# Revit family: Zumtobel PANOS 3 Surface-Mounted R150
name_source: partatom
category: Lighting Fixtures
units: mm (PartAtom-declared; Revit-internal decimal feet)

## family parameters
Cut with Voids When Loaded = Yes
Host = Face
Light Source = Yes
Maintain Annotation Orientation = No
Part Type = Normal
Room Calculation Point = Yes
Round Connector Dimension = Use Diameter
Shared = No

## types (27) — shared parameters
Assembly Code = Pr_70_70_48
Color Filter = 16777215
Description = Downlight, Ceiling surface mounted luminaire
Dimming Lamp Color Temperature Shift = <None>
Emit Shape Visible in Rendering = No
Emit from Circle Diameter = 90 mm  [stored 0.295276 ft]
Lamp = LED
Luminaire Length = 139 mm  [stored 0.456037 ft]
Luminaire Width = 139 mm  [stored 0.456037 ft]
Manufacturer = Zumtobel Lighting
Tilt Angle = -90.00°
URL = https://www.zumtobel.com
zero-valued in all types: Default Elevation

## per-type parameters (varying)
| type | Apparent Load | Housing H | Housing L | Luminaire Height | Material Housing | Material Housing Top | Material Reflector | Model | Photometric Web File | Power Factor | Type Image |
| PANOS SC R150 1k-940 LDO H AL BK | 10 VA | Yes | No | 156 mm  [stored 0.511811 ft] | Zumtobel-Aluminium-RAL 9005-Jet Black | Zumtobel-Aluminium-RAL 9005-Jet Black | Zumtobel-Plastic-RAL 7016-Anthracite Grey-Reflective | 62930183 | 62930183_(STD_LEO).IES | 0.8 | ZS_PA3_F_SM_R150_L_AL_BKBK.jpg |
| PANOS SC R150 1k-940 LDO H AL WH | 10 VA | Yes | No | 156 mm  [stored 0.511811 ft] | Zumtobel-Aluminium-RAL 9003-Signal White | Zumtobel-Aluminium-RAL 9003-Signal White | Zumtobel-Plastic-RAL 7016-Anthracite Grey-Reflective | 62930165 | 62930165_(STD_LEO).IES | 0.8 | ZS_PA3_F_SM_R150_L_AL_WHWH.jpg |
| PANOS SC R150 1k-940 LDO H SPC BK | 10 VA | Yes | No | 156 mm  [stored 0.511811 ft] | Zumtobel-Aluminium-RAL 9005-Jet Black | Zumtobel-Aluminium-RAL 9005-Jet Black | Zumtobel-Plastic-RAL 7001-Silver Grey | 62930192 | 62930192_(STD_LEO).IES | 0.8 | ZS_PA3_F_SM_R150_H_SPC_BKBK.jpg |
| PANOS SC R150 1k-940 LDO H SPC WH | 10 VA | Yes | No | 156 mm  [stored 0.511811 ft] | Zumtobel-Aluminium-RAL 9003-Signal White | Zumtobel-Aluminium-RAL 9003-Signal White | Zumtobel-Plastic-RAL 7001-Silver Grey | 62930174 | 62930174_(STD_LEO).IES | 0.8 | ZS_PA3_F_SM_R150_H_SPC_WHWH.jpg |
| PANOS SC R150 1k-940 LDO L AL BK | 10 VA | No | Yes | 118 mm | Zumtobel-Aluminium-RAL 9005-Jet Black | Zumtobel-Aluminium-RAL 9005-Jet Black | Zumtobel-Plastic-RAL 7016-Anthracite Grey-Reflective | 62930177 | 62930177_(STD_LEO).IES | 0.8 | ZS_PA3_F_SM_R150_L_AL_BKBK.jpg |
| PANOS SC R150 1k-940 LDO L AL WH | 10 VA | No | Yes | 118 mm | Zumtobel-Aluminium-RAL 9003-Signal White | Zumtobel-Aluminium-RAL 9003-Signal White | Zumtobel-Plastic-RAL 7016-Anthracite Grey-Reflective | 60819411 | 60819411_(STD_LEO).IES | 0.8 | ZS_PA3_F_SM_R150_L_AL_WHWH.jpg |
| PANOS SC R150 1k-940 LDO L SPC BK | 10 VA | No | Yes | 118 mm | Zumtobel-Aluminium-RAL 9005-Jet Black | Zumtobel-Aluminium-RAL 9005-Jet Black | Zumtobel-Plastic-RAL 7001-Silver Grey | 62930186 | 62930186_(STD_LEO).IES | 0.8 | ZS_PA3_F_SM_R150_L_SPC_BKBK.jpg |
| PANOS SC R150 1k-940 LDO L SPC WH | 10 VA | No | Yes | 118 mm | Zumtobel-Aluminium-RAL 9003-Signal White | Zumtobel-Aluminium-RAL 9003-Signal White | Zumtobel-Plastic-RAL 7001-Silver Grey | 62930168 | 62930168_(STD_LEO).IES | 0.8 | ZS_PA3_F_SM_R150_L_SPC_WHWH.jpg |
| PANOS SC R150 2k-940 LDO H AL BK | 17 VA | Yes | No | 156 mm  [stored 0.511811 ft] | Zumtobel-Aluminium-RAL 9005-Jet Black | Zumtobel-Aluminium-RAL 9005-Jet Black | Zumtobel-Plastic-RAL 7016-Anthracite Grey-Reflective | 62930184 | 62930184_(STD_LEO).IES | 0.92 | ZS_PA3_F_SM_R150_H_AL_BKBK.jpg |
| PANOS SC R150 2k-940 LDO H AL WH | 17 VA | Yes | No | 156 mm  [stored 0.511811 ft] | Zumtobel-Aluminium-RAL 9003-Signal White | Zumtobel-Aluminium-RAL 9003-Signal White | Zumtobel-Plastic-RAL 7016-Anthracite Grey-Reflective | 62930166 | 62930166_(STD_LEO).IES | 0.92 | ZS_PA3_F_SM_R150_H_AL_WHWH.jpg |
| PANOS SC R150 2k-940 LDO H SPC BK | 17 VA | Yes | No | 156 mm  [stored 0.511811 ft] | Zumtobel-Aluminium-RAL 9005-Jet Black | Zumtobel-Aluminium-RAL 9005-Jet Black | Zumtobel-Plastic-RAL 7001-Silver Grey | 62930193 | 62930193_(STD_LEO).IES | 0.92 | ZS_PA3_F_SM_R150_H_SPC_BKBK.jpg |
| PANOS SC R150 2k-940 LDO H SPC WH | 17 VA | Yes | No | 156 mm  [stored 0.511811 ft] | Zumtobel-Aluminium-RAL 9003-Signal White | Zumtobel-Aluminium-RAL 9003-Signal White | Zumtobel-Plastic-RAL 7001-Silver Grey | 62930175 | 62930175_(STD_LEO).IES | 0.92 | ZS_PA3_F_SM_R150_H_SPC_WHWH.jpg |
| PANOS SC R150 2k-940 LDO L AL BK | 17 VA | No | Yes | 118 mm | Zumtobel-Aluminium-RAL 9005-Jet Black | Zumtobel-Aluminium-RAL 9005-Jet Black | Zumtobel-Plastic-RAL 7016-Anthracite Grey-Reflective | 62930178 | 62930178_(STD_LEO).IES | 0.92 | ZS_PA3_F_SM_R150_L_AL_BKBK.jpg |
| PANOS SC R150 2k-940 LDO L AL WH | 17 VA | No | Yes | 118 mm | Zumtobel-Aluminium-RAL 9003-Signal White | Zumtobel-Aluminium-RAL 9003-Signal White | Zumtobel-Plastic-RAL 7016-Anthracite Grey-Reflective | 60819412 | 60819412_(STD_LEO).IES | 0.92 | ZS_PA3_F_SM_R150_L_AL_WHWH.jpg |
| PANOS SC R150 2k-940 LDO L SPC BK | 17 VA | No | Yes | 118 mm | Zumtobel-Aluminium-RAL 9005-Jet Black | Zumtobel-Aluminium-RAL 9005-Jet Black | Zumtobel-Plastic-RAL 7001-Silver Grey | 62930187 | 62930187_(STD_LEO).IES | 0.92 | ZS_PA3_F_SM_R150_L_SPC_BKBK.jpg |
| PANOS SC R150 2k-940 LDO L SPC WH | 17 VA | No | Yes | 118 mm | Zumtobel-Aluminium-RAL 9003-Signal White | Zumtobel-Aluminium-RAL 9003-Signal White | Zumtobel-Plastic-RAL 7001-Silver Grey | 62930169 | 62930169_(STD_LEO).IES | 0.92 | ZS_PA3_F_SM_R150_L_SPC_WHWH.jpg |
| PANOS SC R150 3k-930 LDO H BK WH | 25 VA | Yes | No | 156 mm  [stored 0.511811 ft] | Zumtobel-Aluminium-RAL 9003-Signal White | Zumtobel-Aluminium-RAL 9003-Signal White | Zumtobel-Plastic-RAL 9005-Jet Black | 62930305 | 62930305_(STD_LEO).IES | 0.95 | ZS_PA3_F_SM_R150_H_BK_WHWH.jpg |
| PANOS SC R150 3k-940 LDO H AL BK | 25 VA | Yes | No | 156 mm  [stored 0.511811 ft] | Zumtobel-Aluminium-RAL 9005-Jet Black | Zumtobel-Aluminium-RAL 9005-Jet Black | Zumtobel-Plastic-RAL 7016-Anthracite Grey-Reflective | 62930185 | 62930185_(STD_LEO).IES | 0.95 | ZS_PA3_F_SM_R150_H_AL_BKBK.jpg |
| PANOS SC R150 3k-940 LDO H AL WH | 25 VA | Yes | No | 156 mm  [stored 0.511811 ft] | Zumtobel-Aluminium-RAL 9003-Signal White | Zumtobel-Aluminium-RAL 9003-Signal White | Zumtobel-Plastic-RAL 7016-Anthracite Grey-Reflective | 62930167 | 62930167_(STD_LEO).IES | 0.95 | ZS_PA3_F_SM_R150_H_AL_WHWH.jpg |
| PANOS SC R150 3k-940 LDO H SPC BK | 25 VA | Yes | No | 156 mm  [stored 0.511811 ft] | Zumtobel-Aluminium-RAL 9005-Jet Black | Zumtobel-Aluminium-RAL 9005-Jet Black | Zumtobel-Plastic-RAL 7001-Silver Grey | 62930194 | 62930194_(STD_LEO).IES | 0.95 | ZS_PA3_F_SM_R150_H_SPC_BKBK.jpg |
| PANOS SC R150 3k-940 LDO H SPC WH | 25 VA | Yes | No | 156 mm  [stored 0.511811 ft] | Zumtobel-Aluminium-RAL 9003-Signal White | Zumtobel-Aluminium-RAL 9003-Signal White | Zumtobel-Plastic-RAL 7001-Silver Grey | 62930176 | 62930176_(STD_LEO).IES | 0.95 | ZS_PA3_F_SM_R150_H_SPC_WHWH.jpg |
| PANOS SC R150 3k-930 LDO L AL WH | 25 VA | No | Yes | 118 mm | Zumtobel-Aluminium-RAL 9003-Signal White | Zumtobel-Aluminium-RAL 9003-Signal White | Zumtobel-Plastic-RAL 7016-Anthracite Grey-Reflective | 62930216 | 62930216_(STD_LEO).IES | 0.95 | ZS_PA3_F_SM_R150_L_AL_WHWH.jpg |
| PANOS SC R150 3k-930 LDO L BK BK | 25 VA | No | Yes | 118 mm | Zumtobel-Aluminium-RAL 9005-Jet Black | Zumtobel-Aluminium-RAL 9005-Jet Black | Zumtobel-Plastic-RAL 9005-Jet Black | 62930303 | 62930303_(STD_LEO).IES | 0.95 | ZS_PA3_F_SM_R150_L_BK_BKBK.jpg |
| PANOS SC R150 3k-940 LDO L AL BK | 25 VA | No | Yes | 118 mm | Zumtobel-Aluminium-RAL 9005-Jet Black | Zumtobel-Aluminium-RAL 9005-Jet Black | Zumtobel-Plastic-RAL 7016-Anthracite Grey-Reflective | 62930179 | 62930179_(STD_LEO).IES | 0.95 | ZS_PA3_F_SM_R150_L_AL_BKBK.jpg |
| PANOS SC R150 3k-940 LDO L AL WH | 25 VA | No | Yes | 118 mm | Zumtobel-Aluminium-RAL 9003-Signal White | Zumtobel-Aluminium-RAL 9003-Signal White | Zumtobel-Plastic-RAL 7016-Anthracite Grey-Reflective | 60819413 | 60819413_(STD_LEO).IES | 0.95 | ZS_PA3_F_SM_R150_L_AL_WHWH.jpg |
| PANOS SC R150 3k-940 LDO L SPC BK | 25 VA | No | Yes | 118 mm | Zumtobel-Aluminium-RAL 9005-Jet Black | Zumtobel-Aluminium-RAL 9005-Jet Black | Zumtobel-Plastic-RAL 7001-Silver Grey | 62930188 | 62930188_(STD_LEO).IES | 0.95 | ZS_PA3_F_SM_R150_L_SPC_BKBK.jpg |
| PANOS SC R150 3k-940 LDO L SPC WH | 25 VA | No | Yes | 118 mm | Zumtobel-Aluminium-RAL 9003-Signal White | Zumtobel-Aluminium-RAL 9003-Signal White | Zumtobel-Plastic-RAL 7001-Silver Grey | 62930170 | 62930170_(STD_LEO).IES | 0.95 | ZS_PA3_F_SM_R150_L_SPC_WHWH.jpg |

note: [stored X ft] marks values corroborated as IEEE doubles in the binary element streams (Revit-internal decimal feet)

## geometry (parser evidence)
native form markers: Sweep x3
no freeform markers — native parametric forms only
